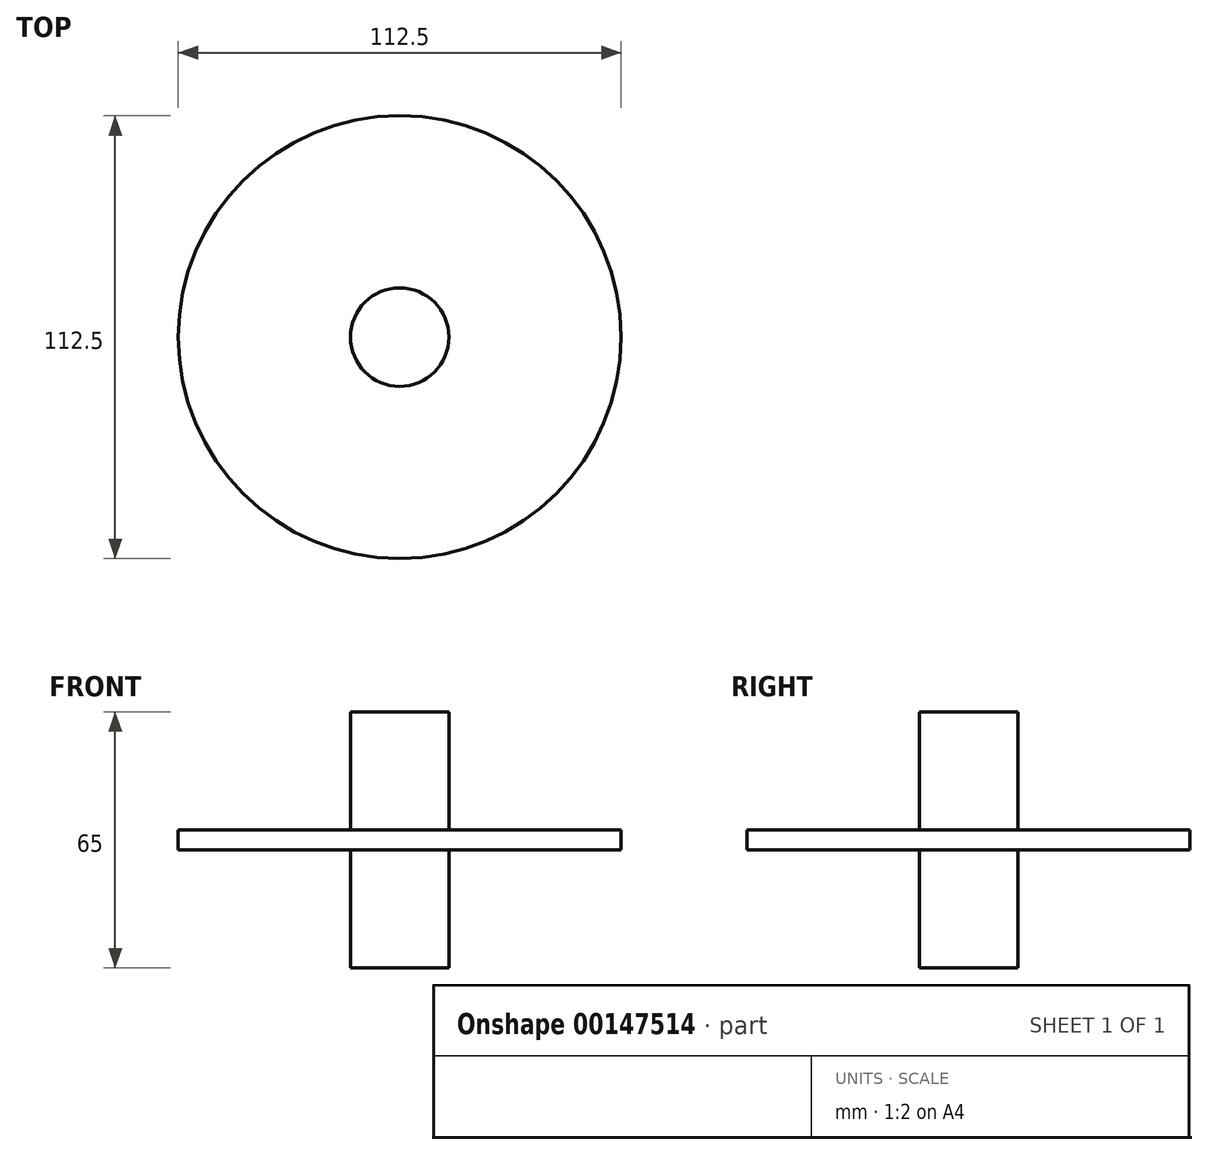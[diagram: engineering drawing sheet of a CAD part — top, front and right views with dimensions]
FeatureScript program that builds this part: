
annotation { "Feature Type Name" : "Feature", "Feature Type Description" : "" }
export const myFeature = defineFeature(function(context is Context, id is Id, definition is map)
    precondition{}
    {
        {
            var Q0;
            Q0=qCreatedBy(makeId("Top.planeOp"),FACE);
            var sketch = newSketch(context, id + "F0", { "sketchPlane" : qUnion([Q0])});
            skCircle(sketch, "E0", {"center": v(0, 0) * mm, "radius": 12.5 * mm});
            skSolve(sketch);
        }
        {
            var Q0;
            Q0=makeQuery(id+"F0.imprint","IMPRINT",FACE,{"disambiguationData":[TD([[makeQuery(id+"F0.imprint","IMPRINT",EDGE,{"derivedFrom":sQuery(id+"F0.wireOp",EDGE,"E0")}),1.0]])]});
            extrude(context, id + "F1", {"entities" : qUnion([Q0]), "depth" : 30 * mm});
        }
        {
            var Q0;
            Q0=makeQuery(id+"F1.opExtrude","CAP_FACE",FACE,{"disambiguationData":[OSD([sQuery(id+"F0.wireOp",EDGE,"E0")])],"isStart":false});
            var sketch = newSketch(context, id + "F2", { "sketchPlane" : qUnion([Q0])});
            skCircle(sketch, "E1", {"center": v(0, 0) * mm, "radius": 56.25 * mm});
            skSolve(sketch);
        }
        {
            var Q0;
            Q0 = qSketchRegion(id + "F2", true);
            extrude(context, id + "F3", {"entities" : qUnion([Q0]), "operationType" : NewBodyOperationType.ADD, "depth" : 5 * mm});
        }
        {
            var Q0;
            Q0=makeQuery(id+"F3.opExtrude","CAP_FACE",FACE,{"disambiguationData":[OSD([sQuery(id+"F2.wireOp",EDGE,"E1")])],"isStart":false});
            var sketch = newSketch(context, id + "F4", { "sketchPlane" : qUnion([Q0])});
            skCircle(sketch, "E2", {"center": v(0, 0) * mm, "radius": 12.5 * mm});
            skSolve(sketch);
        }
        {
            var Q0;
            Q0 = qSketchRegion(id + "F4", true);
            extrude(context, id + "F5", {"entities" : qUnion([Q0]), "operationType" : NewBodyOperationType.ADD, "depth" : 30 * mm});
        }
    });
